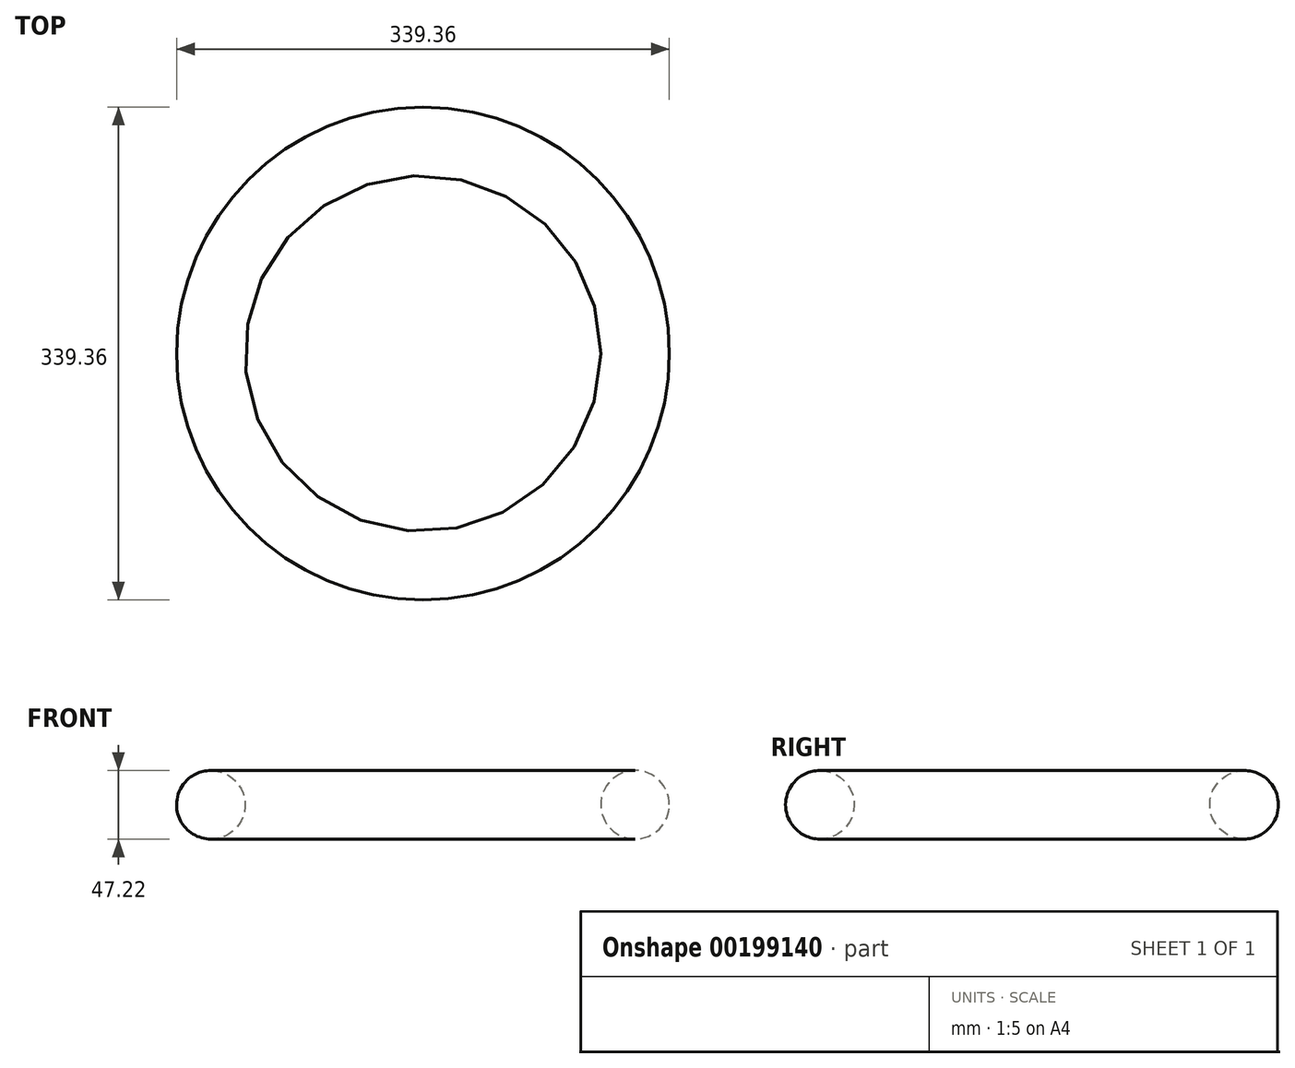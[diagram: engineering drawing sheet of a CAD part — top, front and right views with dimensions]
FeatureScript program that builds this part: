
annotation { "Feature Type Name" : "Feature", "Feature Type Description" : "" }
export const myFeature = defineFeature(function(context is Context, id is Id, definition is map)
    precondition{}
    {
        {
            var Q0;
            Q0=qCreatedBy(makeId("Front.planeOp"),FACE);
            var sketch = newSketch(context, id + "F0", { "sketchPlane" : qUnion([Q0])});
            skCircle(sketch, "E0", {"center": v(-115.4, 0) * mm, "radius": 23.6 * mm});
            skLineSegment(sketch, "E1", {"start": v(30.67, 37.3) * mm, "end": v(30.67, -56.91) * mm});
            skSolve(sketch);
        }
        {
            var Q0;
            Q0=makeQuery(id+"F0.imprint","IMPRINT",FACE,{"disambiguationData":[TD([[makeQuery(id+"F0.imprint","IMPRINT",EDGE,{"derivedFrom":sQuery(id+"F0.wireOp",EDGE,"E0")}),1.0]])]});
            var Q1;
            Q1=sQuery(id+"F0.wireOp",EDGE,"E1");
            revolve(context, id + "F1", {"entities" : qUnion([Q0]), "axis" : qUnion([Q1]), "revolveType" : RevolveType.FULL});
        }
    });
